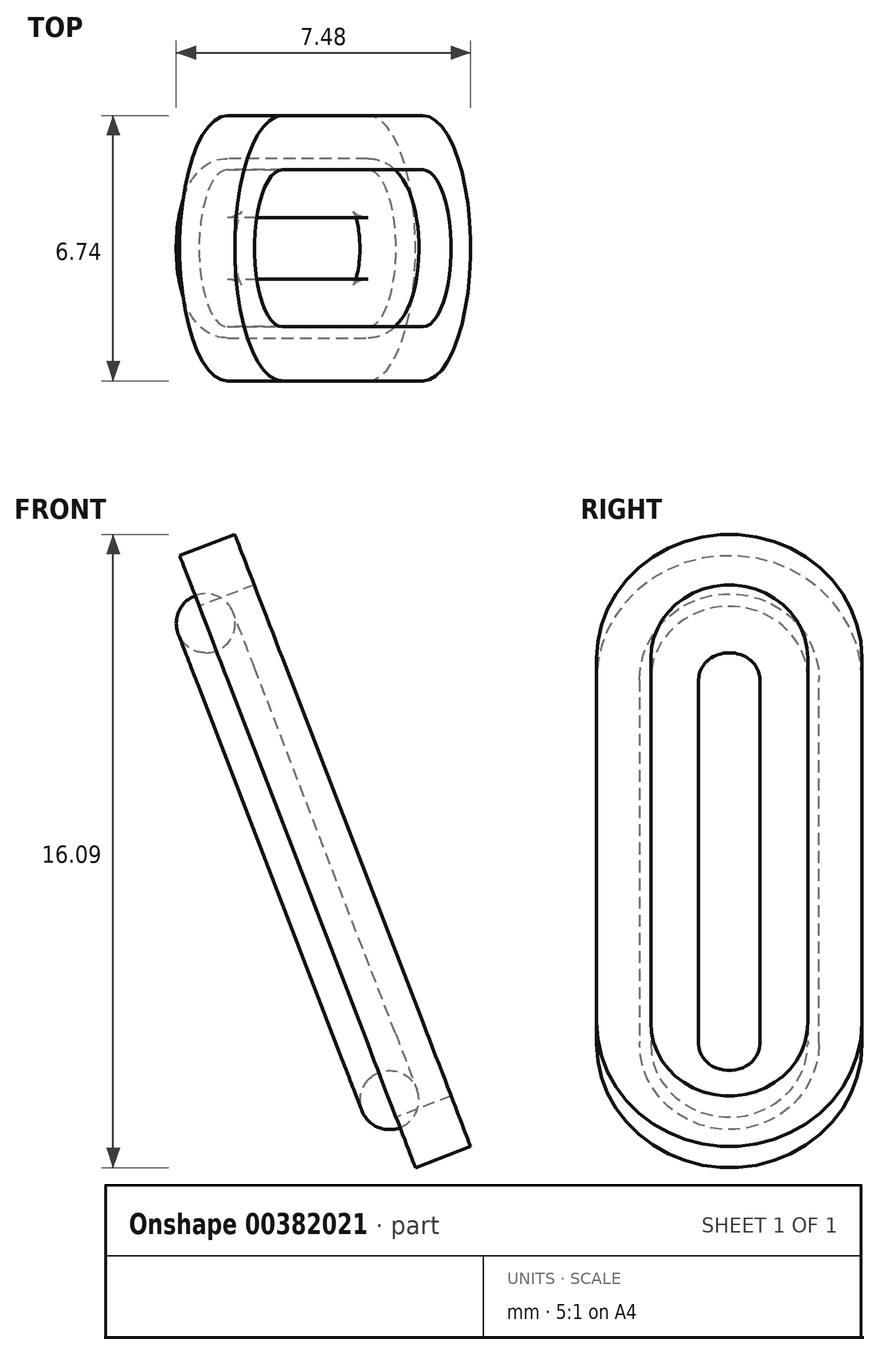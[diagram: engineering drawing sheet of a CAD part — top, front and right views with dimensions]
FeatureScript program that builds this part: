
annotation { "Feature Type Name" : "Feature", "Feature Type Description" : "" }
export const myFeature = defineFeature(function(context is Context, id is Id, definition is map)
    precondition{}
    {
        {
            var Q0;
            Q0=qCreatedBy(makeId("Front.planeOp"),FACE);
            var sketch = newSketch(context, id + "F0", { "sketchPlane" : qUnion([Q0])});
            skLineSegment(sketch, "E0", {"start": v(0, 0) * mm, "end": v(-74.36, 0) * mm, "construction": true});
            skLineSegment(sketch, "E1.MirrorCS", {"start": v(0, 0) * mm, "end": v(74.36, 0) * mm, "construction": true});
            skCircle(sketch, "E2", {"center": v(-2.53, 13.73) * mm, "radius": 0.75 * mm});
            skCircle(sketch, "E3", {"center": v(2.47, 13.73) * mm, "radius": 0.75 * mm});
            skCircle(sketch, "E4", {"center": v(2.47, 0.75) * mm, "radius": 0.75 * mm});
            skCircle(sketch, "E5", {"center": v(-2.53, 0.75) * mm, "radius": 0.75 * mm});
            skLineSegment(sketch, "E6", {"start": v(-2.53, 0.75) * mm, "end": v(2.47, 13.73) * mm, "construction": true});
            skLineSegment(sketch, "E7", {"start": v(2.47, 0.75) * mm, "end": v(-2.53, 13.73) * mm, "construction": true});
            skLineSegment(sketch, "E8", {"start": v(-2.53, 13.73) * mm, "end": v(2.47, 13.73) * mm, "construction": true});
            skLineSegment(sketch, "E9", {"start": v(-1.83, 14) * mm, "end": v(3.17, 1.02) * mm, "construction": true});
            skLineSegment(sketch, "E10", {"start": v(1.72, 13.73) * mm, "end": v(-3.23, 1.02) * mm, "construction": true});
            skPoint(sketch, "E11", {"position": v(-2.53, 14.48) * mm});
            skPoint(sketch, "E12", {"position": v(2.47, 14.48) * mm});
            skSolve(sketch);
        }
        {
            var Q0;
            Q0=sQuery(id+"F0.wireOp",EDGE,"E7");
            cPlane(context, id + "F1", {"entities" : qUnion([Q0]), "cplaneType" : CPlaneType.LINE_ANGLE, "offset" : 25 * mm, "angle" : 0 * degree, "width" : 150 * mm, "height" : 150 * mm});
        }
        {
            var Q0;
            Q0=qCreatedBy(id+"F1.planeOp",FACE);
            var sketch = newSketch(context, id + "F2", { "sketchPlane" : qUnion([Q0])});
            skLineSegment(sketch, "E13", {"start": v(-2, 12.2) * mm, "end": v(-2, 2.27) * mm});
            skLineSegment(sketch, "E14.MirrorCS", {"start": v(2, 12.2) * mm, "end": v(2, 2.27) * mm});
            skArc(sketch, "E15", {"start": v(2, 12.2) * mm, "mid": v(1.41, 13.6) * mm, "end": v(0, 14.2) * mm});
            skArc(sketch, "E16", {"start": v(-2, 2.27) * mm, "mid": v(0, 0.28) * mm, "end": v(2, 2.27) * mm});
            skLineSegment(sketch, "E17", {"start": v(-3.37, 12.2) * mm, "end": v(-3.37, 2.27) * mm});
            skLineSegment(sketch, "E18.MirrorCS", {"start": v(3.37, 12.2) * mm, "end": v(3.37, 2.27) * mm});
            skArc(sketch, "E19", {"start": v(3.37, 12.2) * mm, "mid": v(0, 15.57) * mm, "end": v(-3.37, 12.2) * mm});
            skArc(sketch, "E20", {"start": v(-3.37, 2.27) * mm, "mid": v(0, -1.1) * mm, "end": v(3.37, 2.27) * mm});
            skPoint(sketch, "E21", {"position": v(0, 14.2) * mm});
            skArc(sketch, "E22", {"start": v(0, 14.2) * mm, "mid": v(-1.41, 13.6) * mm, "end": v(-2, 12.2) * mm});
            skSolve(sketch);
        }
        {
            var Q0;
            Q0 = qSketchRegion(id + "F2", true);
            extrude(context, id + "F3", {"entities" : qUnion([Q0]), "depth" : 1.5 * mm});
        }
        {
            var Q0;
            Q0=makeQuery(id+"F0.imprint","IMPRINT",FACE,{"disambiguationData":[TD([[makeQuery(id+"F0.imprint","IMPRINT",EDGE,{"derivedFrom":sQuery(id+"F0.wireOp",EDGE,"E2")}),1.0]])]});
            var Q1;
            Q1=sQuery(id+"F2.wireOp",EDGE,"E15");
            var Q2;
            Q2=sQuery(id+"F2.wireOp",EDGE,"E14.MirrorCS");
            var Q3;
            Q3=sQuery(id+"F2.wireOp",EDGE,"E16");
            var Q4;
            Q4=sQuery(id+"F2.wireOp",EDGE,"E13");
            var Q5;
            Q5=sQuery(id+"F2.wireOp",EDGE,"E22");
            sweep(context, id + "F4", {"profiles" : qUnion([Q0]), "path" : qUnion([Q1, Q2, Q3, Q4, Q5])});
        }
        {
            var Q0;
            Q0=sQuery(id+"F0.wireOp",EDGE,"E6");
            cPlane(context, id + "F5", {"entities" : qUnion([Q0]), "cplaneType" : CPlaneType.LINE_ANGLE, "offset" : 25 * mm, "angle" : 60 * degree, "width" : 150 * mm, "height" : 150 * mm});
        }
    });
